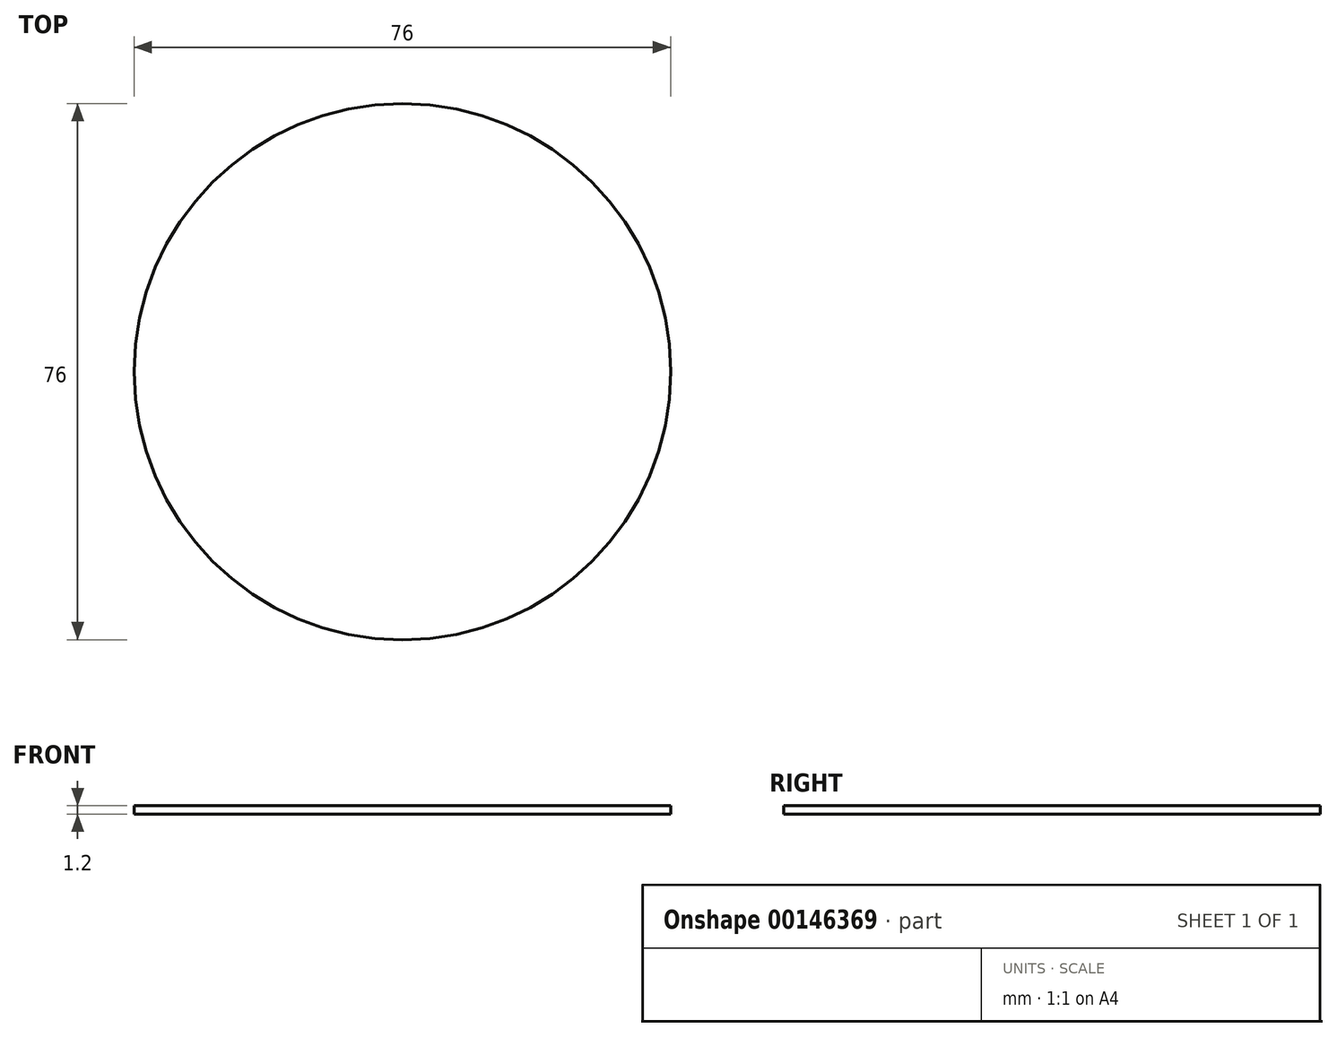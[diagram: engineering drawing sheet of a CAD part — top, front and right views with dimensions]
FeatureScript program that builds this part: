
annotation { "Feature Type Name" : "Feature", "Feature Type Description" : "" }
export const myFeature = defineFeature(function(context is Context, id is Id, definition is map)
    precondition{}
    {
        {
            var Q0;
            Q0=qCreatedBy(makeId("Top.planeOp"),FACE);
            var sketch = newSketch(context, id + "F0", { "sketchPlane" : qUnion([Q0])});
            skCircle(sketch, "E0", {"center": v(0, 0) * mm, "radius": 38 * mm});
            skSolve(sketch);
        }
        {
            var Q0;
            Q0 = qSketchRegion(id + "F0", true);
            extrude(context, id + "F1", {"entities" : qUnion([Q0]), "depth" : 1.2 * mm});
        }
    });
